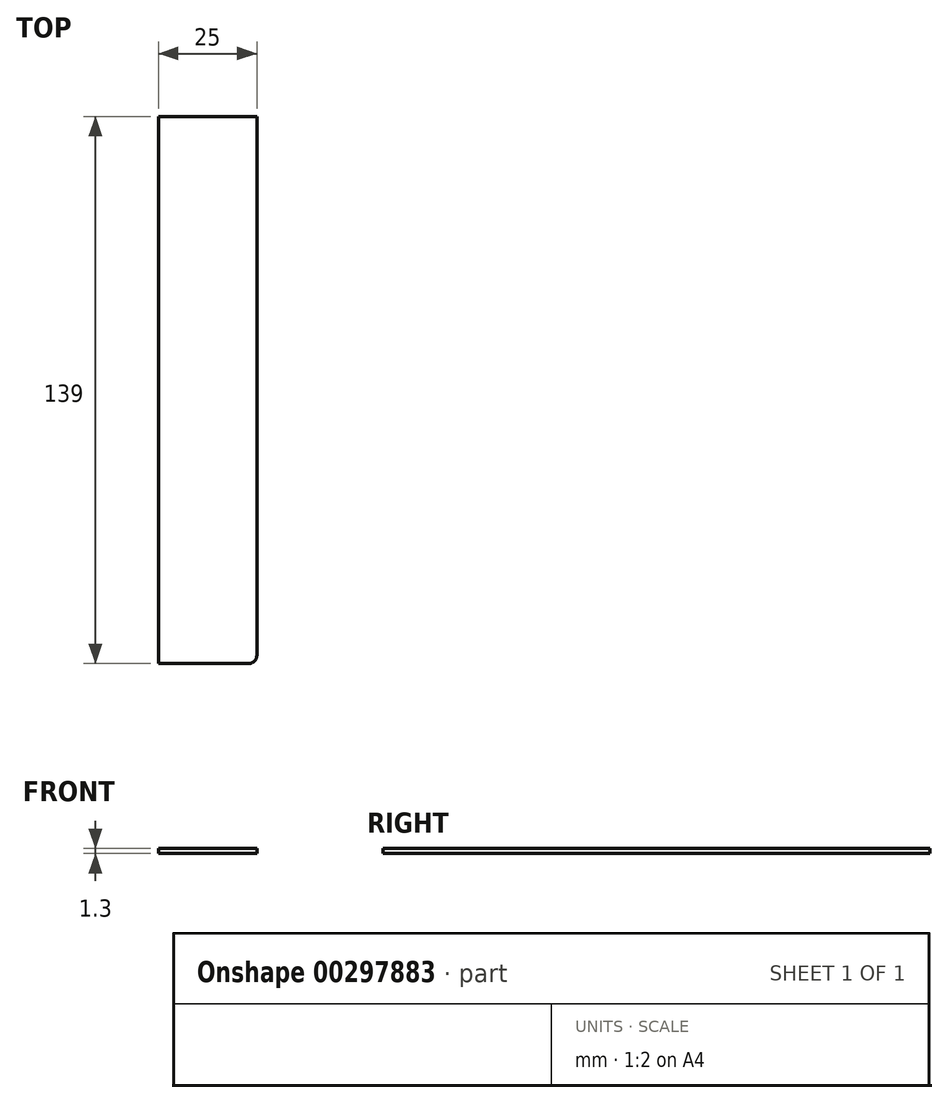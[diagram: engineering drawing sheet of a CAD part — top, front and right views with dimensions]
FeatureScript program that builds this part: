
annotation { "Feature Type Name" : "Feature", "Feature Type Description" : "" }
export const myFeature = defineFeature(function(context is Context, id is Id, definition is map)
    precondition{}
    {
        {
            var Q0;
            Q0=qCreatedBy(makeId("Top.planeOp"),FACE);
            var sketch = newSketch(context, id + "F0", { "sketchPlane" : qUnion([Q0])});
            skLineSegment(sketch, "E0.bottom", {"start": v(12.5, -69.5) * mm, "end": v(-12.5, -69.5) * mm});
            skLineSegment(sketch, "E0.top", {"start": v(12.5, 69.5) * mm, "end": v(-12.5, 69.5) * mm});
            skLineSegment(sketch, "E0.left", {"start": v(12.5, -69.5) * mm, "end": v(12.5, 69.5) * mm});
            skLineSegment(sketch, "E0.right", {"start": v(-12.5, -69.5) * mm, "end": v(-12.5, 69.5) * mm});
            skPoint(sketch, "E0.middle", {"position": v(0, 0) * mm});
            skSolve(sketch);
        }
        {
            var Q0;
            Q0 = qSketchRegion(id + "F0", true);
            extrude(context, id + "F1", {"entities" : qUnion([Q0]), "depth" : 1.3 * mm});
        }
        {
            var Q0;
            Q0=makeQuery(id+"F1.opExtrude","SWEPT_EDGE",EDGE,{"disambiguationData":[OSD([sQuery(id+"F0.wireOp",EDGE,"E0.bottom"),sQuery(id+"F0.wireOp",EDGE,"E0.left")])]});
            fillet(context, id + "F2", {"entities" : qUnion([Q0]), "radius" : 2 * mm, "tangentPropagation" : true, "allowEdgeOverflow" : false});
        }
    });
